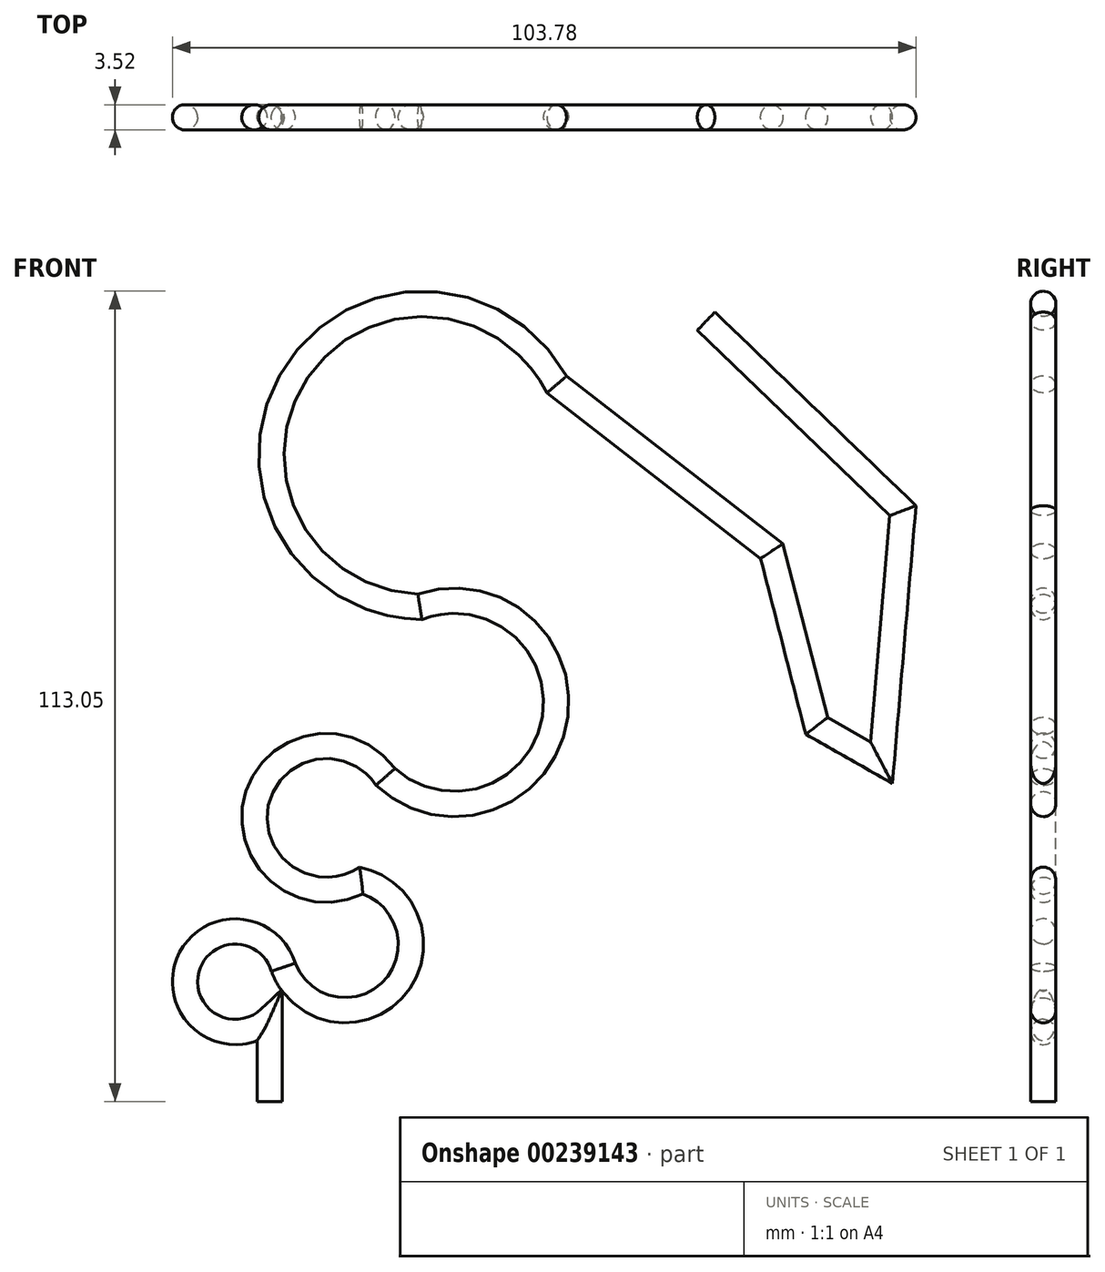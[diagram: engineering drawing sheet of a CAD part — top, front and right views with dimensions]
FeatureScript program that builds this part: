
annotation { "Feature Type Name" : "Feature", "Feature Type Description" : "" }
export const myFeature = defineFeature(function(context is Context, id is Id, definition is map)
    precondition{}
    {
        {
            var Q0;
            Q0=qCreatedBy(makeId("Front.planeOp"),FACE);
            var sketch = newSketch(context, id + "F0", { "sketchPlane" : qUnion([Q0])});
            skLineSegment(sketch, "E0", {"start": v(0, 0) * mm, "end": v(0, 11.6) * mm});
            skArc(sketch, "E1", {"start": v(1.9, 18.73) * mm, "mid": v(-11.58, 18.52) * mm, "end": v(0, 11.6) * mm});
            skArc(sketch, "E2", {"start": v(1.9, 18.73) * mm, "mid": v(17.35, 15.76) * mm, "end": v(12.8, 30.81) * mm});
            skArc(sketch, "E3", {"start": v(16.16, 45.28) * mm, "mid": v(-1.88, 41.83) * mm, "end": v(12.8, 30.81) * mm});
            skArc(sketch, "E4", {"start": v(16.16, 45.28) * mm, "mid": v(39.7, 52.86) * mm, "end": v(20.96, 69.01) * mm});
            skArc(sketch, "E5", {"start": v(40.06, 100.03) * mm, "mid": v(3.37, 101.23) * mm, "end": v(20.96, 69.01) * mm});
            skLineSegment(sketch, "E6", {"start": v(40.06, 100.03) * mm, "end": v(70.06, 76.77) * mm});
            skLineSegment(sketch, "E7", {"start": v(70.06, 76.77) * mm, "end": v(76.34, 52.39) * mm});
            skLineSegment(sketch, "E8", {"start": v(76.34, 52.39) * mm, "end": v(85.4, 47.25) * mm});
            skLineSegment(sketch, "E9", {"start": v(85.4, 47.25) * mm, "end": v(88.38, 82.43) * mm});
            skLineSegment(sketch, "E10", {"start": v(88.38, 82.43) * mm, "end": v(60.9, 108.87) * mm});
            skSolve(sketch);
        }
        {
            var Q0;
            Q0=qCreatedBy(makeId("Top.planeOp"),FACE);
            var sketch = newSketch(context, id + "F1", { "sketchPlane" : qUnion([Q0])});
            skCircle(sketch, "E11", {"center": v(0, 0) * mm, "radius": 1.76 * mm});
            skSolve(sketch);
        }
        {
            var Q0;
            Q0 = qSketchRegion(id + "F1", true);
            var Q1;
            Q1 = qConstructionFilter(qBodyType(qCreatedBy(id + "F0" ,EDGE), BodyType.WIRE), ConstructionObject.NO);
            sweep(context, id + "F2", {"profiles" : qUnion([Q0]), "path" : qUnion([Q1])});
        }
    });
